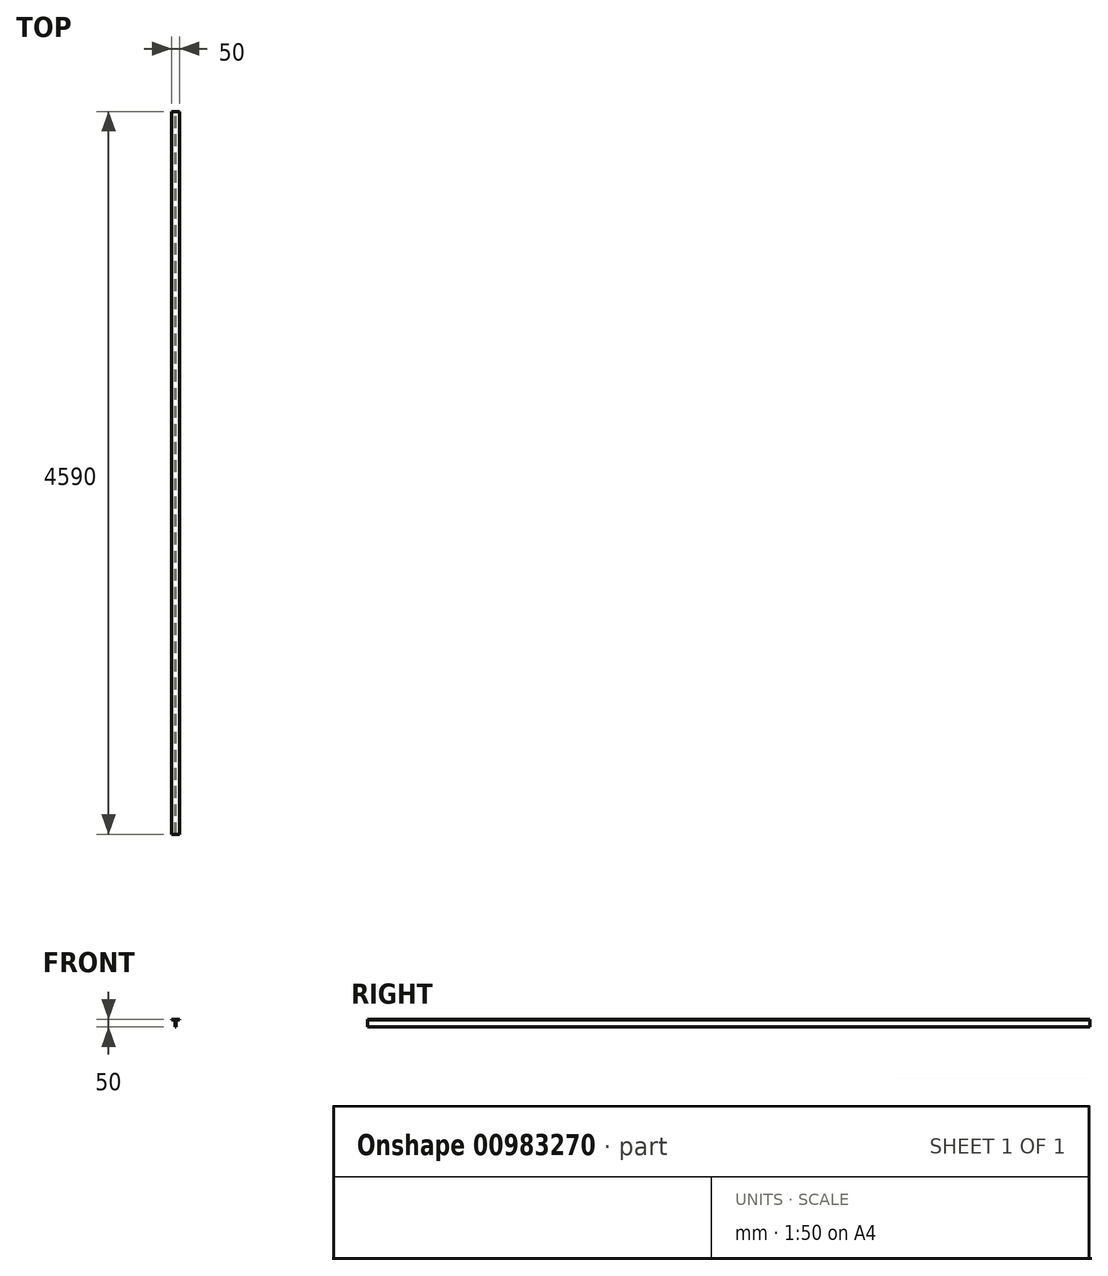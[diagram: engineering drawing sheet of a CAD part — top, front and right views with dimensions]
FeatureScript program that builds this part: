
annotation { "Feature Type Name" : "Feature", "Feature Type Description" : "" }
export const myFeature = defineFeature(function(context is Context, id is Id, definition is map)
    precondition{}
    {
        {
            var Q0;
            Q0=qCreatedBy(makeId("Front.planeOp"),FACE);
            var sketch = newSketch(context, id + "F0", { "sketchPlane" : qUnion([Q0])});
            skLineSegment(sketch, "E0", {"start": v(-69.8, 0) * mm, "end": v(-69.8, 45) * mm});
            skLineSegment(sketch, "E1", {"start": v(-69.8, 45) * mm, "end": v(-91.73, 45) * mm});
            skLineSegment(sketch, "E2", {"start": v(-91.73, 45) * mm, "end": v(-91.73, 50) * mm});
            skLineSegment(sketch, "E3", {"start": v(-91.73, 50) * mm, "end": v(-41.73, 50) * mm});
            skLineSegment(sketch, "E4", {"start": v(-41.73, 50) * mm, "end": v(-41.73, 45) * mm});
            skLineSegment(sketch, "E5", {"start": v(-41.73, 45) * mm, "end": v(-64.8, 45) * mm});
            skLineSegment(sketch, "E6", {"start": v(-64.8, 45) * mm, "end": v(-64.8, 0) * mm});
            skLineSegment(sketch, "E7", {"start": v(-64.8, 0) * mm, "end": v(-69.8, 0) * mm});
            skSolve(sketch);
        }
        {
            var Q0;
            Q0=makeQuery(id+"F0.imprint","IMPRINT",FACE,{"disambiguationData":[TD([[makeQuery(id+"F0.imprint","IMPRINT",EDGE,{"derivedFrom":sQuery(id+"F0.wireOp",EDGE,"E0")}),-1.0]])]});
            extrude(context, id + "F1", {"entities" : qUnion([Q0]), "depth" : 4590 * mm, "offsetDistance" : 25 * mm});
        }
    });
